# Revit family: Building-ConnessioniIEC309-GEWISS-67IB-PRESE-INTERBLOCCATE_IP67_CON_FONDO
name_source: partatom
category: Apparecchi elettrici
units: mm (PartAtom-declared; Revit-internal decimal feet)

## family parameters
Condiviso = Sì
Host = Superficie
Mantenere orientamento annotazione = Sì
Punto di calcolo locali = Sì
Quota connettore circolare = Usa diametro
Taglio con vuoti quando caricato = Sì
Tipo di parte = Normale

## types (23) — shared parameters
Catalogo = BUILDING
Catalogo Serie = 67 IB
Codice Electrocod = 2222
Con fondo = Si
Corpo presa = GEWISS -BLU
Frequenza = 50/60 Hz
Frequenza nominale (Hz) = 50/60 Hz
Glow Wire Test = 850 °C (Presa IB) - 650 °C (Cassetta di fondo)
Glow wire test: = 850 °C (Presa IB) - 650 °C (Cassetta di fondo)
Grado di protezione = IP67
IDF = 2488cdfe-ec7b-4723-8311-f4c1a43a8eac
IDT = 80fd8aa3-f4ad-4bf9-871a-178f60767a59
Immagine tipo = E.jpg
Produttore = GEWISS S.p.A.
Prospetto di default = 1219 mm
Protezione = NO (SBF)
Resistenza agli urti = IK08
SEO = Presa
Scheda Tecnica = https://www.gewiss.com
Simbolo presa = PRESAINDSTAGNA : 3P
Struttura = Grigio RAL - 7035
Temperatura di funzionamento = -25 ÷ +40 °C
Temperatura di utilizzo = -25 +40 °C
Termopressione con biglia = 125 °C (Presa IB) - 80 °C (Cassetta di fondo)
Tipologia = Verticale
URL = https://www.gewiss.com
Versione file RFA = 21.4
presa = Giallo
zero-valued in all types: giallo

## per-type parameters (varying)
| type | Codice EAN | Colore | Colore: | Corrente nominale (A) | Corrente nominale (In) | Descrizione | Modello | N. poli | Numero di poli | Riferimento h | Tensione nominale | Tensione nominale: |
| GW66213N - PR.BL IP67 C.F.3P+T 32A 110V 4H SBF | 8011564741256 | Giallo | Giallo | 32 | 32 | PR.BL IP67 C.F.3P+T 32A 110V 4H SBF | GW66213N | 3P+T | 3P+T | 4 | 100 - 130 V | 100 - 130 V |
| GW66205N - PR.BL IP67 C.F.3P+T 16A 230V 9H SBF | 8011564741188 | Blu | Blu | 16 | 16 | PR.BL IP67 C.F.3P+T 16A 230V 9H SBF | GW66205N | 3P+T | 3P+T | 9 | 200 - 250 V | 200 - 250 V |
| GW66202N - PR.BL IP67 C.F.3P+T 16A 110V 4H SBF | 8011564741157 | Giallo | Giallo | 16 | 16 | PR.BL IP67 C.F.3P+T 16A 110V 4H SBF | GW66202N | 3P+T | 3P+T | 4 | 100 - 130 V | 100 - 130 V |
| GW66204N - PR.BL IP67 C.F.2P+T 16A 230V 6H SBF | 8011564741171 | Blu | Blu | 16 | 16 | PR.BL IP67 C.F.2P+T 16A 230V 6H SBF | GW66204N | 2P+T | 2P+T | 6 | 200 - 250 V | 200 - 250 V |
| GW66209N - PR.BL IP67 C.F.3P+N+T 16A 400V 6H SBF | 8011564742512 | Rosso | Rosso | 16 | 16 | PR.BL IP67 C.F.3P+N+T 16A 400V 6H SBF | GW66209N | 3P+N+T | 3P+N+T | 6 | 380 - 415 V | 380 - 415 V |
| GW66210N - PR.BL IP67 C.F.3P+T 16A 500V 7H SBF | 8011564741225 | Nero | Nero | 16 | 16 | PR.BL IP67 C.F.3P+T 16A 500V 7H SBF | GW66210N | 3P+T | 3P+T | 7 | 480 - 500 V | 480 - 500 V |
| GW66215N - PR.BL IP67 C.F.2P+T 32A 230V 6H SBF | 8011564742529 | Blu | Blu | 32 | 32 | PR.BL IP67 C.F.2P+T 32A 230V 6H SBF | GW66215N | 2P+T | 2P+T | 6 | 200 - 250 V | 200 - 250 V |
| GW66222N - PR.BL IP67 C.F.3P+N+T 32A 500V 7H SBF | 8011564741324 | Nero | Nero | 32 | 32 | PR.BL IP67 C.F.3P+N+T 32A 500V 7H SBF | GW66222N | 3P+N+T | 3P+N+T | 7 | 480 - 500 V | 480 - 500 V |
| GW66219N - PR.BL IP67 C.F.3P+T 32A 400V 6H SBF | 8011564741300 | Rosso | Rosso | 32 | 32 | PR.BL IP67 C.F.3P+T 32A 400V 6H SBF | GW66219N | 3P+T | 3P+T | 6 | 380 - 415 V | 380 - 415 V |
| GW66211N - PR.BL IP67 C.F.3P+N+T 16A 500V 7H SBF | 8011564741232 | Nero | Nero | 16 | 16 | PR.BL IP67 C.F.3P+N+T 16A 500V 7H SBF | GW66211N | 3P+N+T | 3P+N+T | 7 | 480 - 500 V | 480 - 500 V |
| GW66216N - PR.BL IP67 C.F.3P+T 32A 230V 9H SBF | 8011564741270 | Blu | Blu | 32 | 32 | PR.BL IP67 C.F.3P+T 32A 230V 9H SBF | GW66216N | 3P+T | 3P+T | 9 | 200 - 250 V | 200 - 250 V |
| GW66208N - PR.BL IP67 C.F.3P+T 16A 400V 6H SBF | 8011564741218 | Rosso | Rosso | 16 | 16 | PR.BL IP67 C.F.3P+T 16A 400V 6H SBF | GW66208N | 3P+T | 3P+T | 6 | 380 - 415 V | 380 - 415 V |
| GW66214N - PR.BL IP67 C.F.3P+N+T 32A 110V 4H SBF | 8011564741263 | Giallo | Giallo | 32 | 32 | PR.BL IP67 C.F.3P+N+T 32A 110V 4H SBF | GW66214N | 3P+N+T | 3P+N+T | 4 | 100 - 130 V | 100 - 130 V |
| GW66206N - PR.BL IP67 C.F.3P+N+T 16A 230V 9H SBF | 8011564741195 | Blu | Blu | 16 | 16 | PR.BL IP67 C.F.3P+N+T 16A 230V 9H SBF | GW66206N | 3P+N+T | 3P+N+T | 9 | 200 - 250 V | 200 - 250 V |
| GW66212N - PR.BL IP67 C.F.2P+T 32A 110V 4H SBF | 8011564741249 | Giallo | Giallo | 32 | 32 | PR.BL IP67 C.F.2P+T 32A 110V 4H SBF | GW66212N | 2P+T | 2P+T | 4 | 100 - 130 V | 100 - 130 V |
| GW66218N - PR.BL IP67 C.F.2P+T 32A 400V 9H SBF | 8011564741294 | Rosso | Rosso | 32 | 32 | PR.BL IP67 C.F.2P+T 32A 400V 9H SBF | GW66218N | 2P+T | 2P+T | 9 | 380 - 415 V | 380 - 415 V |
| GW66201N - PR.BL IP67 C.F.2P+T 16A 110V 4H SBF | 8011564741140 | Giallo | Giallo | 16 | 16 | PR.BL IP67 C.F.2P+T 16A 110V 4H SBF | GW66201N | 2P+T | 2P+T | 4 | 100 - 130 V | 100 - 130 V |
| GW66257N - PR.BL IP67 C.F.3P+T 32A 380V 3H SBF | 8011564741522 | Rosso | Rosso | 32 | 32 | PR.BL IP67 C.F.3P+T 32A 380V 3H SBF | GW66257N | 3P+T | 3P+T | 3 | 380 - 440 V | 380 - 440 V |
| GW66207N - PR.BL IP67 C.F.2P+T 16A 400V 9H SBF | 8011564741201 | Rosso | Rosso | 16 | 16 | PR.BL IP67 C.F.2P+T 16A 400V 9H SBF | GW66207N | 2P+T | 2P+T | 9 | 380 - 415 V | 380 - 415 V |
| GW66203N - PR.BL IP67 C.F.3P+N+T 16A 110V 4H SBF | 8011564741164 | Giallo | Giallo | 16 | 16 | PR.BL IP67 C.F.3P+N+T 16A 110V 4H SBF | GW66203N | 3P+N+T | 3P+N+T | 4 | 100 - 130 V | 100 - 130 V |
| GW66221N - PR.BL IP67 C.F.3P+T 32A 500V 7H SBF | 8011564741317 | Nero | Nero | 32 | 32 | PR.BL IP67 C.F.3P+T 32A 500V 7H SBF | GW66221N | 3P+T | 3P+T | 7 | 480 - 500 V | 480 - 500 V |
| GW66217N - PR.BL IP67 C.F.3P+N+T 32A 230V 9H SBF | 8011564741287 | Blu | Blu | 32 | 32 | PR.BL IP67 C.F.3P+N+T 32A 230V 9H SBF | GW66217N | 3P+N+T | 3P+N+T | 9 | 200 - 250 V | 200 - 250 V |
| GW66220N - PR.BL IP67 C.F.3P+N+T 32A 400V 6H SBF | 8011564742536 | Rosso | Rosso | 32 | 32 | PR.BL IP67 C.F.3P+N+T 32A 400V 6H SBF | GW66220N | 3P+N+T | 3P+N+T | 6 | 380 - 415 V | 380 - 415 V |

## geometry (parser evidence)
native form markers: Sweep x5
no freeform markers — native parametric forms only
